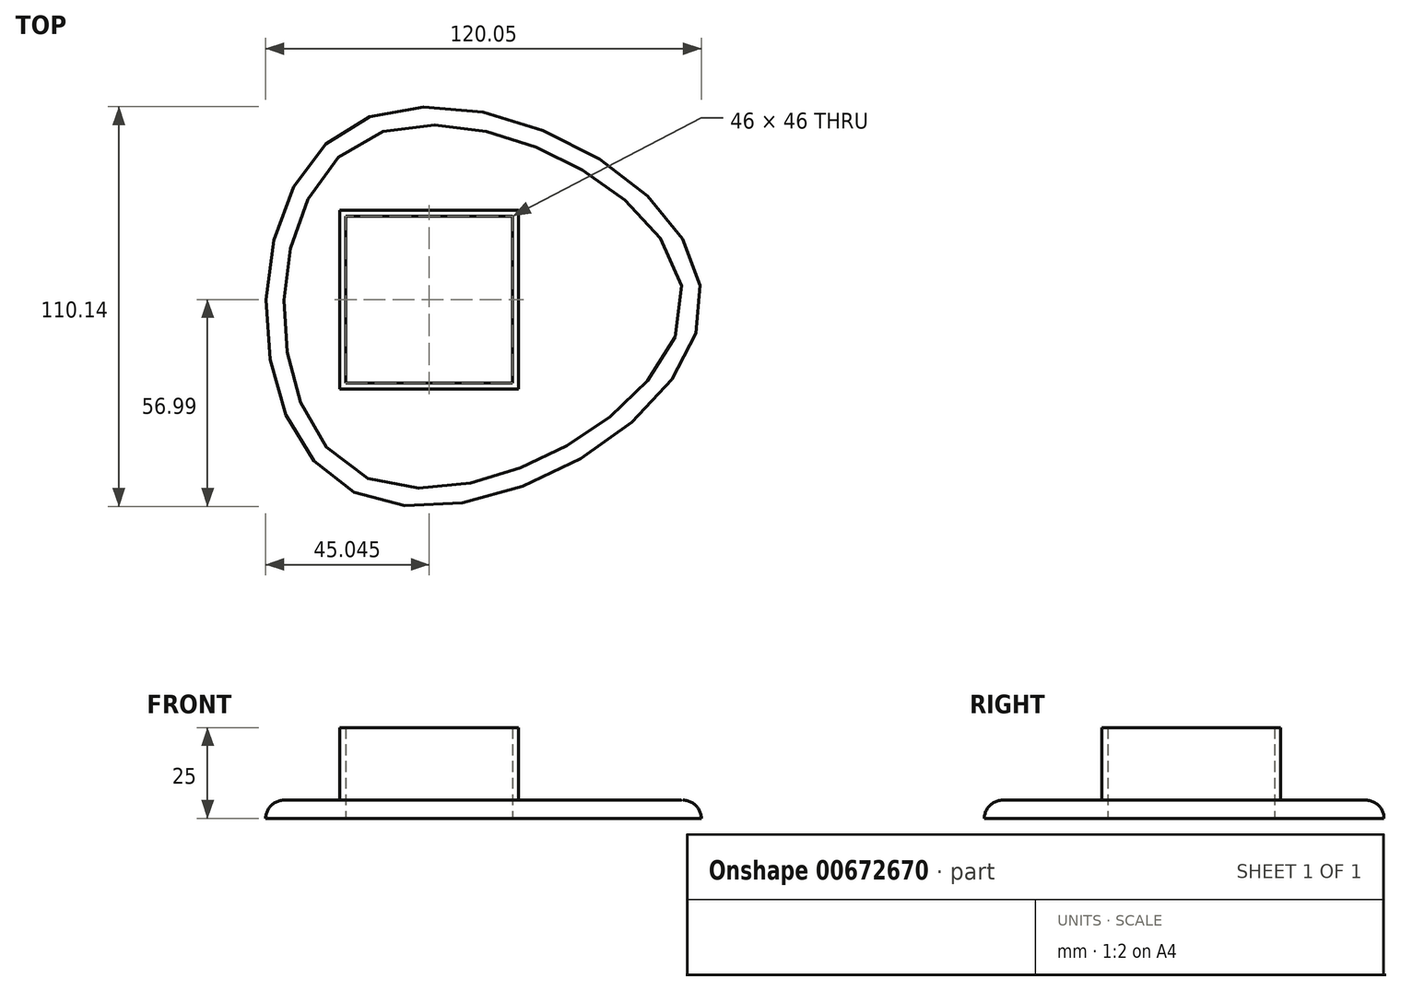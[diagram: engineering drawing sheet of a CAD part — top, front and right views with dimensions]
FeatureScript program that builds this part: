
annotation { "Feature Type Name" : "Feature", "Feature Type Description" : "" }
export const myFeature = defineFeature(function(context is Context, id is Id, definition is map)
    precondition{}
    {
        {
            var Q0;
            Q0=qCreatedBy(makeId("Top.planeOp"),FACE);
            var sketch = newSketch(context, id + "F0", { "sketchPlane" : qUnion([Q0])});
            skFitSpline(sketch, "E0", {"points": [v(0, 47.68) * mm, v(97.15, 0) * mm, v(0, -52.32) * mm, v(0, 47.68) * mm]});
            skLineSegment(sketch, "E1", {"start": v(0, 47.68) * mm, "end": v(0, -52.32) * mm, "construction": true});
            skLineSegment(sketch, "E2", {"start": v(97.15, 0) * mm, "end": v(-22.85, 0) * mm, "construction": true});
            skPoint(sketch, "E3", {"position": v(37.15, 0) * mm});
            skLineSegment(sketch, "E4", {"start": v(37.15, 0) * mm, "end": v(-22.85, 0) * mm});
            skPoint(sketch, "E5", {"position": v(7.15, 0) * mm});
            skLineSegment(sketch, "E6", {"start": v(37.15, 0) * mm, "end": v(7.15, 0) * mm});
            skPoint(sketch, "E7", {"position": v(22.15, 0) * mm});
            skLineSegment(sketch, "E8.bottom", {"start": v(46.75, 24.6) * mm, "end": v(-2.45, 24.6) * mm});
            skLineSegment(sketch, "E8.top", {"start": v(46.75, -24.6) * mm, "end": v(-2.45, -24.6) * mm});
            skLineSegment(sketch, "E8.left", {"start": v(46.75, 24.6) * mm, "end": v(46.75, -24.6) * mm});
            skLineSegment(sketch, "E8.right", {"start": v(-2.45, 24.6) * mm, "end": v(-2.45, -24.6) * mm});
            skLineSegment(sketch, "E9.bottom", {"start": v(45.15, -23) * mm, "end": v(-0.85, -23) * mm});
            skLineSegment(sketch, "E9.top", {"start": v(45.15, 23) * mm, "end": v(-0.85, 23) * mm});
            skLineSegment(sketch, "E9.left", {"start": v(45.15, -23) * mm, "end": v(45.15, 23) * mm});
            skLineSegment(sketch, "E9.right", {"start": v(-0.85, -23) * mm, "end": v(-0.85, 23) * mm});
            skLineSegment(sketch, "E10", {"start": v(45.15, -23) * mm, "end": v(46.75, -23) * mm, "construction": true});
            skSolve(sketch);
        }
        {
            var Q0;
            Q0=makeQuery(id+"F0.imprint","IMPRINT",FACE,{"disambiguationData":[TD([[makeQuery(id+"F0.imprint","IMPRINT",EDGE,{"derivedFrom":sQuery(id+"F0.wireOp",EDGE,"E0")}),-1.0]])]});
            extrude(context, id + "F1", {"entities" : qUnion([Q0]), "depth" : 5 * mm, "offsetDistance" : 25 * mm});
        }
        {
            var Q0;
            {var subQ1=sQuery(id+"F0.wireOp",EDGE,"E8.bottom");Q0=makeQuery(id+"F0.imprint","IMPRINT",FACE,{"disambiguationData":[TD([[makeQuery(id+"F0.imprint","IMPRINT",EDGE,{"derivedFrom":subQ1}),1.0]])]});}
            extrude(context, id + "F2", {"entities" : qUnion([Q0]), "operationType" : NewBodyOperationType.ADD, "depth" : 25 * mm, "offsetDistance" : 25 * mm});
        }
        {
            var Q0;
            Q0=makeQuery(id+"F1.opExtrude","CAP_EDGE",EDGE,{"disambiguationData":[OSD([sQuery(id+"F0.wireOp",EDGE,"E8.left")])],"isStart":false});
            var Q1;
            Q1=makeQuery(id+"F1.opExtrude","CAP_EDGE",EDGE,{"disambiguationData":[OSD([sQuery(id+"F0.wireOp",EDGE,"E8.top")])],"isStart":false});
            var Q2;
            Q2=makeQuery(id+"F1.opExtrude","CAP_EDGE",EDGE,{"disambiguationData":[OSD([sQuery(id+"F0.wireOp",EDGE,"E8.right")])],"isStart":false});
            var Q3;
            Q3=makeQuery(id+"F1.opExtrude","CAP_EDGE",EDGE,{"disambiguationData":[OSD([sQuery(id+"F0.wireOp",EDGE,"E8.bottom")])],"isStart":false});
            var Q4;
            Q4=makeQuery(id+"F1.opExtrude","CAP_EDGE",EDGE,{"disambiguationData":[OSD([sQuery(id+"F0.wireOp",EDGE,"E0")])],"isStart":false});
            fillet(context, id + "F3", {"entities" : qUnion([Q0, Q1, Q2, Q3, Q4]), "radius" : 5 * mm, "tangentPropagation" : true, "allowEdgeOverflow" : false});
        }
    });
